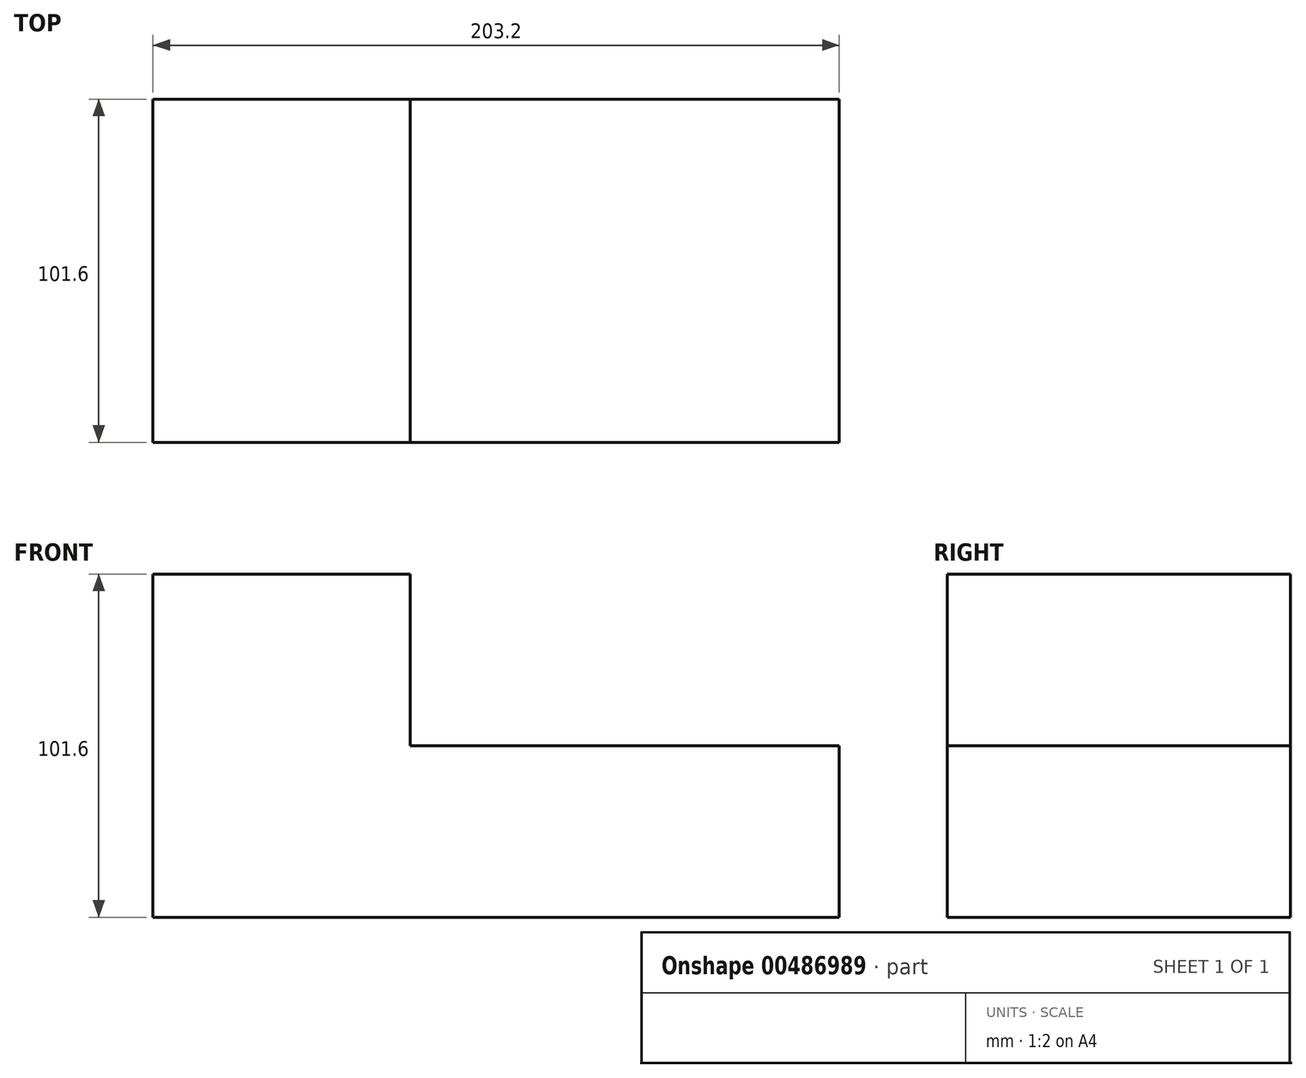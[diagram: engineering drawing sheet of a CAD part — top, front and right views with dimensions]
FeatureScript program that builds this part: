
annotation { "Feature Type Name" : "Feature", "Feature Type Description" : "" }
export const myFeature = defineFeature(function(context is Context, id is Id, definition is map)
    precondition{}
    {
        {
            var Q0;
            Q0=qCreatedBy(makeId("Front.planeOp"),FACE);
            var sketch = newSketch(context, id + "F0", { "sketchPlane" : qUnion([Q0])});
            skLineSegment(sketch, "E0.bottom", {"start": v(0, 0) * mm, "end": v(-76.2, 0) * mm});
            skLineSegment(sketch, "E0.top", {"start": v(0, 101.6) * mm, "end": v(-76.2, 101.6) * mm});
            skLineSegment(sketch, "E0.left", {"start": v(0, 0) * mm, "end": v(0, 101.6) * mm});
            skLineSegment(sketch, "E0.right", {"start": v(-76.2, 0) * mm, "end": v(-76.2, 101.6) * mm});
            skLineSegment(sketch, "E1.bottom", {"start": v(0, 0) * mm, "end": v(127, 0) * mm});
            skLineSegment(sketch, "E1.top", {"start": v(0, 50.8) * mm, "end": v(127, 50.8) * mm});
            skLineSegment(sketch, "E1.left", {"start": v(0, 0) * mm, "end": v(0, 50.8) * mm});
            skLineSegment(sketch, "E1.right", {"start": v(127, 0) * mm, "end": v(127, 50.8) * mm});
            skSolve(sketch);
        }
        {
            var Q0;
            Q0 = qSketchRegion(id + "F0", true);
            extrude(context, id + "F1", {"entities" : qUnion([Q0]), "depth" : 101.6 * mm});
        }
    });
